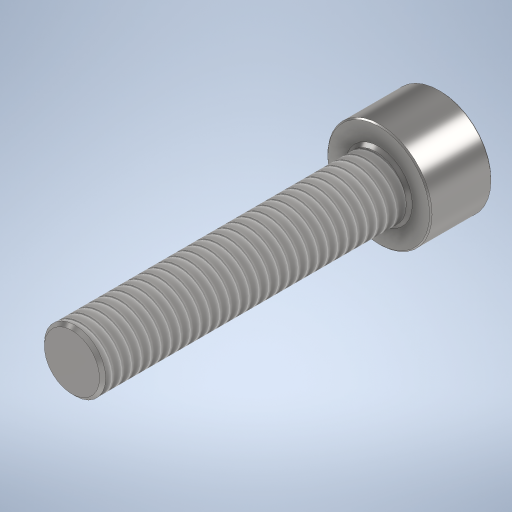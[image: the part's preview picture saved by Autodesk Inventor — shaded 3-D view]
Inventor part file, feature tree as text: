
AUTODESK INVENTOR PART (.ipt)
format: ipt  version: 2024 (Build 280153000, 153)  size: 329,728 bytes
history: native  units: mm
features: extrude x3, chamfer x3, sketch x2, thread x1, hole x1
ambient origin geometry x8: Origin, YZ Plane, XZ Plane, XY Plane, X Axis, Y Axis, Z Axis, Center Point
bodies: Solid1 (feature_tree)
feature tree (10):
  sketch  "Sketch1"  dims[d0=8.5mm d1=5.0mm]
  extrude  "Extrusion1"  Depth=5.0mm
  extrude  "Extrusion2"  Depth=2.5mm TaperAngle=0.0deg
  thread  "Thread1"  [1 undecoded]
  chamfer  "Chamfer1"  Distance=0.1mm Angle=45.0deg
  sketch  "Sketch2"  dims[d2=25.0mm d3=0.0mm d4=5.0mm d5=0.0mm d6=15.0mm d7=0.0mm d8=0.1mm d9=2.0mm d10=45.0deg d11=3.75mm d12=4.0mm d15=0.5mm d16=2.0mm d17=45.0deg d18=3.0mm d19=0.0mm d20=0.25mm d21=2.0mm d22=45.0deg d23=3.75mm d24=6.0mm d25=4.0mm d26=2.0mm d27=90.0deg d28=2.5mm d29=150.0deg]
  hole  "Hole1"  [1 undecoded]
  chamfer  "Chamfer2"  Distance=4.0mm
  extrude  "Extrusion4"  Depth=2.5mm TaperAngle=45.0deg
  chamfer  "Chamfer3"  Distance=3.0mm
note: 2 required parameter values undecoded (feature->parameter linkage not recoverable at this tier; creation-order binding heuristic only, values carry confidence <= 0.55)
